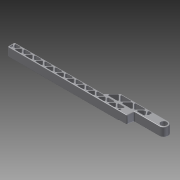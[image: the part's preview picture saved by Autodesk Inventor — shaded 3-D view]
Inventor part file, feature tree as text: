
AUTODESK INVENTOR PART (.ipt)
format: ipt  version: 2011 SP2 (Build 150309200, 309)  size: 967,680 bytes
history: native  units: mm
features: fillet x13, extrude x9, projected_geometry x8, sketch x7, plane x1, mirror x1
ambient origin geometry x8: Origin, YZ Plane, XZ Plane, XY Plane, X Axis, Y Axis, Z Axis, Center Point
feature tree (39):
  sketch  "Sketch1"  dims[d14=1.0mm d16=1.0mm]
  extrude  "Extrusion11"  Depth=1.0mm
  extrude  "Extrusion12"  Depth=1.0mm
  extrude  "Extrusion13"  Depth=16.580628mm
  extrude  "Extrusion14"  Depth=0.5mm
  extrude  "Extrusion15"  Depth=0.5mm
  extrude  "Extrusion16"  Depth=0.5mm
  fillet  "Fillet13"  Radius=0.5mm
  fillet  "Fillet14"  Radius=0.5mm
  fillet  "Fillet15"  Radius=0.5mm
  fillet  "Fillet16"  Radius=0.5mm
  fillet  "Fillet17"  Radius=0.5mm
  fillet  "Fillet18"  Radius=0.5mm
  fillet  "Fillet19"  Radius=0.5mm
  fillet  "Fillet20"  Radius=0.5mm
  fillet  "Fillet21"  Radius=0.5mm
  fillet  "Fillet22"  Radius=0.5mm
  fillet  "Fillet25"  Radius=0.5mm
  extrude  "Extrusion17"  Depth=0.5mm
  fillet  "Fillet26"  Radius=0.5mm
  extrude  "Extrusion18"  Depth=0.5mm
  fillet  "Fillet27"  Radius=0.5mm
  plane  "Work Plane2"
  mirror  "Mirror2"
  extrude  "Extrusion19"  Depth=0.5mm
  sketch  "Sketch11"  dims[d23=1.0mm d24=1.0mm]
  projected_geometry  "Projected Loop7"
  sketch  "Sketch12"  dims[d25=1.0mm d30=16.580628mm]
  projected_geometry  "Projected Loop8"
  projected_geometry  "Projected Loop9"
  sketch  "Sketch13"  dims[d32=1.0mm d62=0.5mm]
  sketch  "Sketch14"  dims[d64=0.5mm d65=0.5mm]
  sketch  "Sketch15"  dims[d66=0.5mm d68=0.5mm d69=0.5mm d70=0.5mm d71=0.5mm d72=0.5mm d73=0.5mm d74=0.5mm d75=0.5mm d76=0.5mm d77=0.5mm d78=0.5mm d79=0.5mm]
  projected_geometry  "Projected Loop10"
  projected_geometry  "Projected Loop11"
  projected_geometry  "Projected Loop12"
  projected_geometry  "Projected Loop13"
  projected_geometry  "Projected Loop14"
  sketch  "Sketch16"  dims[d80=0.5mm d81=0.5mm d82=0.5mm d83=0.5mm d84=0.5mm d85=0.5mm d86=0.5mm d87=0.5mm d88=0.5mm d89=0.5mm d90=0.5mm d91=0.5mm d92=0.5mm d93=0.5mm d94=0.5mm d95=0.5mm d96=0.5mm d97=0.5mm d98=0.5mm d99=0.5mm d100=0.5mm d101=0.5mm d102=0.5mm d103=0.5mm d104=0.5mm d106=0.5mm d107=0.5mm d108=0.5mm d109=0.5mm d115=14.209mm d116=3.912mm d120=5.45mm d121=3.75mm d122=1.875mm d124=2.725mm d126=3.060539mm d166=1.0mm d167=0.5mm d169=0.5mm d171=0.5mm d172=0.5mm d173=0.5mm d174=0.5mm d175=0.5mm d176=0.5mm d177=0.5mm d178=0.5mm d179=0.5mm d180=0.5mm d181=0.5mm d182=0.5mm d183=13.0mm d184=5.0mm d185=10.0mm d186=3.45mm d187=1.956mm d188=28.816511mm d189=34.516421mm d190=9.0mm d191=1.0mm d192=172.0mm d193=35.152794mm d194=10.0mm d195=0.0mm d196=10.0mm d197=0.0mm d198=6.85mm d199=0.0mm d200=10.0mm d201=8.0mm d202=0.0mm d203=14.835299mm d204=10.0mm d205=0.0mm d206=16.580628mm d207=10.0mm d208=0.0mm d209=1.0mm d210=1.0mm d211=0.5mm d212=1.75mm d213=0.2mm d214=1.0mm d215=0.5mm d216=0.5mm d217=0.5mm d218=1.0mm d221=2.25mm d222=10.0mm d223=0.0mm d224=0.75mm d225=10.0mm d226=0.0mm d227=0.5mm d228=-175.0mm d229=1.0mm d230=11.0mm d231=0.0mm d232=0.0mm]
